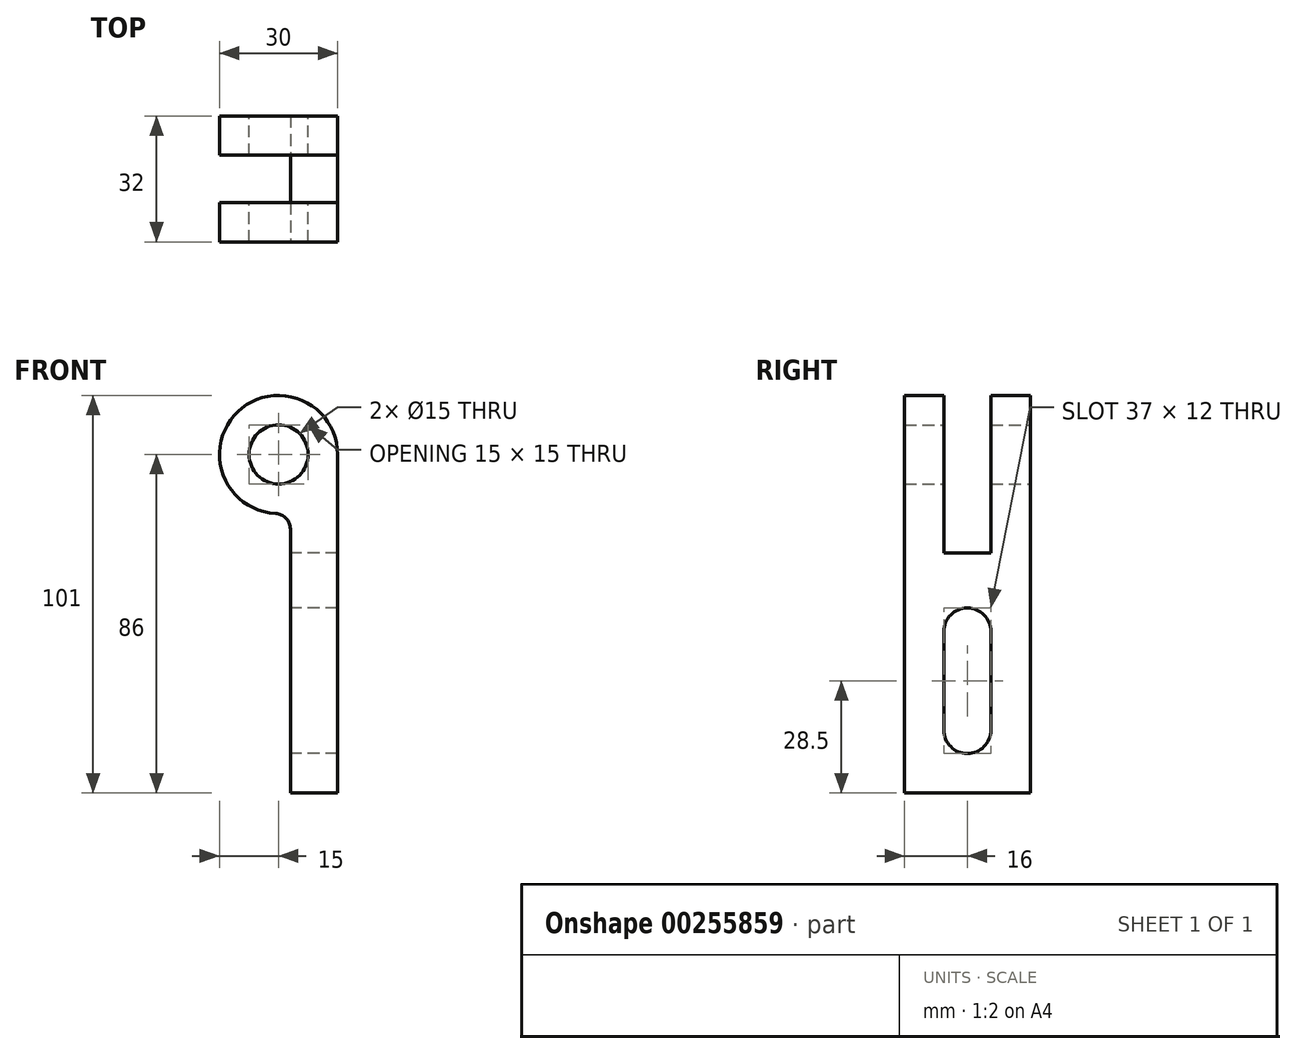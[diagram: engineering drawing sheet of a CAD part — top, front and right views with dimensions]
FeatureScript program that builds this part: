
annotation { "Feature Type Name" : "Feature", "Feature Type Description" : "" }
export const myFeature = defineFeature(function(context is Context, id is Id, definition is map)
    precondition{}
    {
        {
            var Q0;
            Q0=qCreatedBy(makeId("Front.planeOp"),FACE);
            var sketch = newSketch(context, id + "F0", { "sketchPlane" : qUnion([Q0])});
            skArc(sketch, "E0", {"start": v(15, 0) * mm, "mid": v(-11.62, 9.49) * mm, "end": v(3, -14.7) * mm});
            skCircle(sketch, "E1", {"center": v(0, 0) * mm, "radius": 7.5 * mm});
            skLineSegment(sketch, "E2.top", {"start": v(15, -86) * mm, "end": v(3, -86) * mm});
            skLineSegment(sketch, "E2.left", {"start": v(15, 0) * mm, "end": v(15, -86) * mm});
            skLineSegment(sketch, "E2.right", {"start": v(3, -14.7) * mm, "end": v(3, -86) * mm});
            skSolve(sketch);
        }
        {
            var Q0;
            Q0=makeQuery(id+"F0.imprint","IMPRINT",FACE,{"disambiguationData":[TD([[makeQuery(id+"F0.imprint","IMPRINT",EDGE,{"derivedFrom":sQuery(id+"F0.wireOp",EDGE,"E0")}),1.0]])]});
            extrude(context, id + "F1", {"entities" : qUnion([Q0]), "endBound" : BoundingType.SYMMETRIC, "depth" : 32 * mm});
        }
        {
            var Q0;
            Q0=qCreatedBy(makeId("Right.planeOp"),FACE);
            cPlane(context, id + "F2", {"entities" : qUnion([Q0]), "cplaneType" : CPlaneType.OFFSET, "offset" : 25 * mm, "oppositeDirection" : true, "width" : 150 * mm, "height" : 150 * mm});
        }
        {
            var Q0;
            Q0=qCreatedBy(id+"F2.planeOp",FACE);
            var sketch = newSketch(context, id + "F3", { "sketchPlane" : qUnion([Q0])});
            skLineSegment(sketch, "E3.left", {"start": v(6, -45) * mm, "end": v(6, -70) * mm});
            skLineSegment(sketch, "E3.right", {"start": v(-6, -45) * mm, "end": v(-6, -70) * mm});
            skArc(sketch, "E4", {"start": v(6, -45) * mm, "mid": v(0, -39) * mm, "end": v(-6, -45) * mm});
            skArc(sketch, "E5", {"start": v(-6, -70) * mm, "mid": v(0, -76) * mm, "end": v(6, -70) * mm});
            skLineSegment(sketch, "E6.bottom", {"start": v(6, 25) * mm, "end": v(-6, 25) * mm});
            skLineSegment(sketch, "E6.top", {"start": v(6, -25) * mm, "end": v(-6, -25) * mm});
            skLineSegment(sketch, "E6.left", {"start": v(6, 25) * mm, "end": v(6, -25) * mm});
            skLineSegment(sketch, "E6.right", {"start": v(-6, 25) * mm, "end": v(-6, -25) * mm});
            skPoint(sketch, "E6.middle", {"position": v(0, 0) * mm});
            skArc(sketch, "E7", {"start": v(16, -70) * mm, "mid": v(0, -86) * mm, "end": v(-16, -70) * mm});
            skLineSegment(sketch, "E8.0.0", {"start": v(16, -14.7) * mm, "end": v(16, -86) * mm});
            skLineSegment(sketch, "E8.0.1", {"start": v(16, -86) * mm, "end": v(-16, -86) * mm});
            skLineSegment(sketch, "E8.0.2", {"start": v(-16, -86) * mm, "end": v(-16, -14.7) * mm});
            skLineSegment(sketch, "E8.0.3", {"start": v(-16, -14.7) * mm, "end": v(16, -14.7) * mm});
            skSolve(sketch);
        }
        {
            var Q0;
            {var subQ0=sQuery(id+"F3.wireOp",EDGE,"E6.bottom");Q0=makeQuery(id+"F3.imprint","IMPRINT",FACE,{"disambiguationData":[TD([[makeQuery(id+"F3.imprint","IMPRINT",EDGE,{"derivedFrom":subQ0}),1.0]])]});}
            var Q1;
            {var subQ0=sQuery(id+"F3.wireOp",EDGE,"E6.top");Q1=makeQuery(id+"F3.imprint","IMPRINT",FACE,{"disambiguationData":[TD([[makeQuery(id+"F3.imprint","IMPRINT",EDGE,{"derivedFrom":subQ0}),-1.0]])]});}
            var Q2;
            {var subQ0=sQuery(id+"F3.wireOp",EDGE,"E8.0.2");var subQ1=sQuery(id+"F3.wireOp",EDGE,"E7");var subQ2=makeQuery(id+"F3.imprint","INTERSECT",VERTEX,{"derivedFrom":[subQ1,subQ0]});Q2=makeQuery(id+"F3.imprint","IMPRINT",FACE,{"disambiguationData":[TD([[makeQuery(id+"F3.imprint","IMPRINT",EDGE,{"disambiguationData":[TD([[subQ2,1.0]])],"derivedFrom":subQ1}),1.0]])]});}
            var Q3;
            {var subQ0=sQuery(id+"F3.wireOp",EDGE,"E8.0.0");var subQ1=sQuery(id+"F3.wireOp",EDGE,"E7");var subQ2=makeQuery(id+"F3.imprint","INTERSECT",VERTEX,{"derivedFrom":[subQ1,subQ0]});Q3=makeQuery(id+"F3.imprint","IMPRINT",FACE,{"disambiguationData":[TD([[makeQuery(id+"F3.imprint","IMPRINT",EDGE,{"disambiguationData":[TD([[subQ2,-1.0]])],"derivedFrom":subQ1}),1.0]])]});}
            var Q4;
            Q4=makeQuery(id+"F3.imprint","IMPRINT",FACE,{"disambiguationData":[TD([[makeQuery(id+"F3.imprint","IMPRINT",EDGE,{"derivedFrom":sQuery(id+"F3.wireOp",EDGE,"E3.left")}),-1.0]])]});
            extrude(context, id + "F4", {"entities" : qUnion([Q0, Q1, Q2, Q3, Q4]), "operationType" : NewBodyOperationType.REMOVE, "endBound" : BoundingType.THROUGH_ALL, "depth" : 25 * mm});
        }
        {
            var Q0;
            {var subQ0=sQuery(id+"F0.wireOp",EDGE,"E0");var subQ1=sQuery(id+"F0.wireOp",EDGE,"E2.right");Q0=makeQuery(id+"F4.boolean.opBoolean","SPLIT",EDGE,{"disambiguationData":[TD([makeQuery(id+"F4.opExtrude","SWEPT_FACE",FACE,{"disambiguationData":[OSD([sQuery(id+"F3.wireOp",EDGE,"E6.right")])]})])],"derivedFrom":makeQuery(id+"F1.opExtrude","SWEPT_EDGE",EDGE,{"disambiguationData":[OSD([subQ0,subQ1])]})});}
            var Q1;
            {var subQ0=sQuery(id+"F0.wireOp",EDGE,"E0");var subQ1=sQuery(id+"F0.wireOp",EDGE,"E2.right");Q1=makeQuery(id+"F4.boolean.opBoolean","SPLIT",EDGE,{"disambiguationData":[TD([makeQuery(id+"F4.opExtrude","SWEPT_FACE",FACE,{"disambiguationData":[OSD([sQuery(id+"F3.wireOp",EDGE,"E6.left")])]})])],"derivedFrom":makeQuery(id+"F1.opExtrude","SWEPT_EDGE",EDGE,{"disambiguationData":[OSD([subQ0,subQ1])]})});}
            fillet(context, id + "F5", {"entities" : qUnion([Q0, Q1]), "radius" : 4 * mm, "tangentPropagation" : true, "allowEdgeOverflow" : false});
        }
    });
